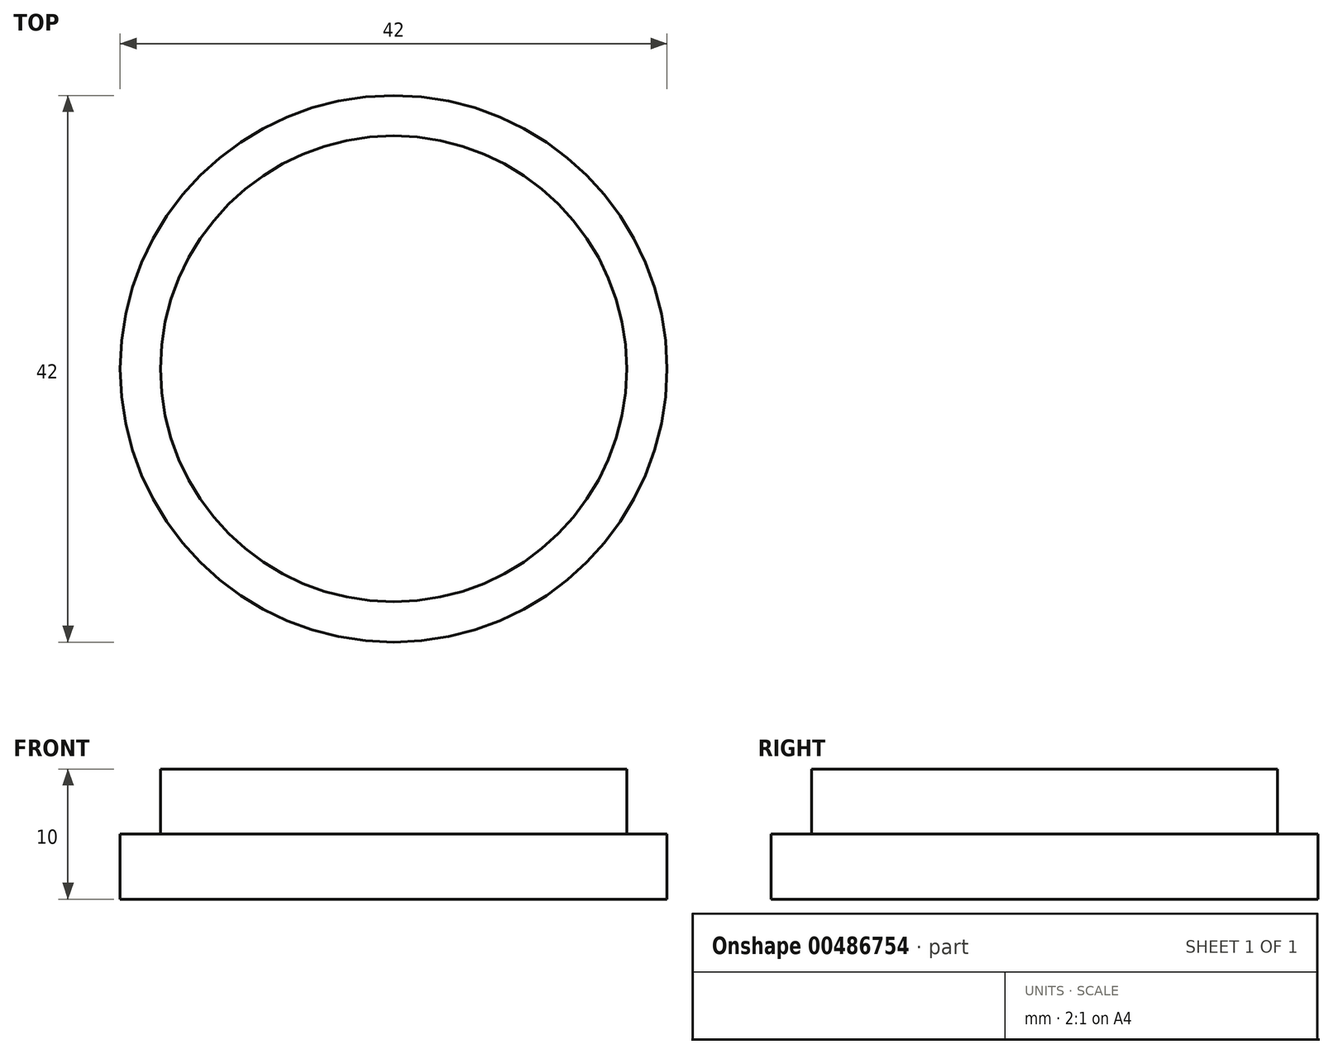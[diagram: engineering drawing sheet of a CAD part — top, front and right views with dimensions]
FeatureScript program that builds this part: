
annotation { "Feature Type Name" : "Feature", "Feature Type Description" : "" }
export const myFeature = defineFeature(function(context is Context, id is Id, definition is map)
    precondition{}
    {
        {
            var Q0;
            Q0=qCreatedBy(makeId("Top.planeOp"),FACE);
            var sketch = newSketch(context, id + "F0", { "sketchPlane" : qUnion([Q0])});
            skCircle(sketch, "E0", {"center": v(0, 0) * mm, "radius": 21 * mm});
            skCircle(sketch, "E1", {"center": v(0, 0) * mm, "radius": 17.9 * mm});
            skSolve(sketch);
        }
        {
            var Q0;
            Q0=qSketchRegion(id+"F0",true);
            var Q1;
            Q1=makeQuery(id+"F0.imprint","IMPRINT",FACE,{"disambiguationData":[TD([[makeQuery(id+"F0.imprint","IMPRINT",EDGE,{"derivedFrom":sQuery(id+"F0.wireOp",EDGE,"E1")}),1.0]])]});
            extrude(context, id + "F1", {"entities" : qUnion([Q0, Q1]), "depth" : 5 * mm, "offsetDistance" : 25 * mm});
        }
        {
            var Q0;
            Q0=makeQuery(id+"F1.opExtrude","CAP_FACE",FACE,{"disambiguationData":[OSD([sQuery(id+"F0.wireOp",EDGE,"E0")])],"isStart":false});
            var sketch = newSketch(context, id + "F2", { "sketchPlane" : qUnion([Q0])});
            skCircle(sketch, "E2", {"center": v(0, 0) * mm, "radius": 17.9 * mm});
            skSolve(sketch);
        }
        {
            var Q0;
            Q0=qSketchRegion(id+"F2",true);
            extrude(context, id + "F3", {"entities" : qUnion([Q0]), "operationType" : NewBodyOperationType.ADD, "depth" : 5 * mm, "offsetDistance" : 25 * mm});
        }
        {
            var Q0;
            Q0=makeQuery(id+"F1.opExtrude","CAP_FACE",FACE,{"disambiguationData":[OSD([sQuery(id+"F0.wireOp",EDGE,"E0")])],"isStart":true});
            var sketch = newSketch(context, id + "F4", { "sketchPlane" : qUnion([Q0])});
            skCircle(sketch, "E3", {"center": v(0, 0) * mm, "radius": 20 * mm});
            skSolve(sketch);
        }
        {
            var Q0;
            Q0=makeQuery(id+"F4.imprint","IMPRINT",FACE,{"disambiguationData":[TD([[makeQuery(id+"F4.imprint","IMPRINT",EDGE,{"derivedFrom":sQuery(id+"F4.wireOp",EDGE,"E3")}),-1.0]])]});
            cPlane(context, id + "F5", {"entities" : qUnion([Q0]), "cplaneType" : CPlaneType.OFFSET, "offset" : 25 * mm, "width" : 150 * mm, "height" : 150 * mm});
        }
        {
            var Q0;
            Q0=qCreatedBy(id+"F5.planeOp",FACE);
            var sketch = newSketch(context, id + "F6", { "sketchPlane" : qUnion([Q0])});
            skCircle(sketch, "E4", {"center": v(0, 0) * mm, "radius": 10 * mm});
            skSolve(sketch);
        }
        {
            var Q0;
            Q0=qSketchRegion(id+"F6",true);
            extrude(context, id + "F7", {"entities" : qUnion([Q0]), "depth" : 25 * mm, "offsetDistance" : 25 * mm});
        }
        {
            var Q0;
            Q0=makeQuery(id+"F4.imprint","IMPRINT",FACE,{"disambiguationData":[TD([[makeQuery(id+"F4.imprint","IMPRINT",EDGE,{"derivedFrom":sQuery(id+"F4.wireOp",EDGE,"E3")}),1.0]])]});
            var Q1;
            Q1=makeQuery(id+"F7.opExtrude","CAP_FACE",FACE,{"disambiguationData":[OSD([sQuery(id+"F6.wireOp",EDGE,"E4")])],"isStart":true});
            loft(context, id + "F8", {"sheetProfilesArray" : [{ "sheetProfileEntities" : qUnion([Q0]) }, { "sheetProfileEntities" : qUnion([Q1]) }]});
        }
        {
            var Q0;
            Q0=qCreatedBy(makeId("Front.planeOp"),FACE);
            var sketch = newSketch(context, id + "F9", { "sketchPlane" : qUnion([Q0])});
            skLineSegment(sketch, "E5.0", {"start": v(10, -50) * mm, "end": v(-10, -50) * mm});
            skLineSegment(sketch, "E6", {"start": v(0, -50) * mm, "end": v(0, -58.92) * mm});
            skFitSpline(sketch, "E7", {"points": [v(0, -58.92) * mm, v(0, -67.57) * mm, v(-5.17, -77.72) * mm, v(-29.04, -98.2) * mm], "startDerivative": vector(2.98, -35.22) * mm, "endDerivative": vector(-59.82, -46.01) * mm});
            skSolve(sketch);
        }
        {
            var Q0;
            Q0=makeQuery(id+"F7.opExtrude","CAP_FACE",FACE,{"disambiguationData":[OSD([sQuery(id+"F6.wireOp",EDGE,"E4")])],"isStart":false});
            var Q1;
            Q1=sQuery(id+"F9.wireOp",EDGE,"E6");
            var Q2;
            Q2=sQuery(id+"F9.wireOp",EDGE,"E7");
            sweep(context, id + "F10", {"operationType" : NewBodyOperationType.ADD, "profiles" : qUnion([Q0]), "path" : qUnion([Q1, Q2])});
        }
        {
            var Q0;
            Q0=makeQuery(id+"F7.opExtrude","SWEPT_BODY",BODY,{"disambiguationData":[OSD([sQuery(id+"F6.wireOp",EDGE,"E4")])]});
            deleteBodies(context, id + "F11", {"entities" : qUnion([Q0])});
        }
        {
            var Q0;
            Q0=makeQuery(id+"F8.opLoft","SWEPT_BODY",BODY,{"disambiguationData":[OSD([makeQuery(id+"F4.imprint","IMPRINT",FACE,{"disambiguationData":[TD([[makeQuery(id+"F4.imprint","IMPRINT",EDGE,{"derivedFrom":sQuery(id+"F4.wireOp",EDGE,"E3")}),1.0]])]}),sQuery(id+"F6.wireOp",EDGE,"E4")])]});
            deleteBodies(context, id + "F12", {"entities" : qUnion([Q0])});
        }
    });
